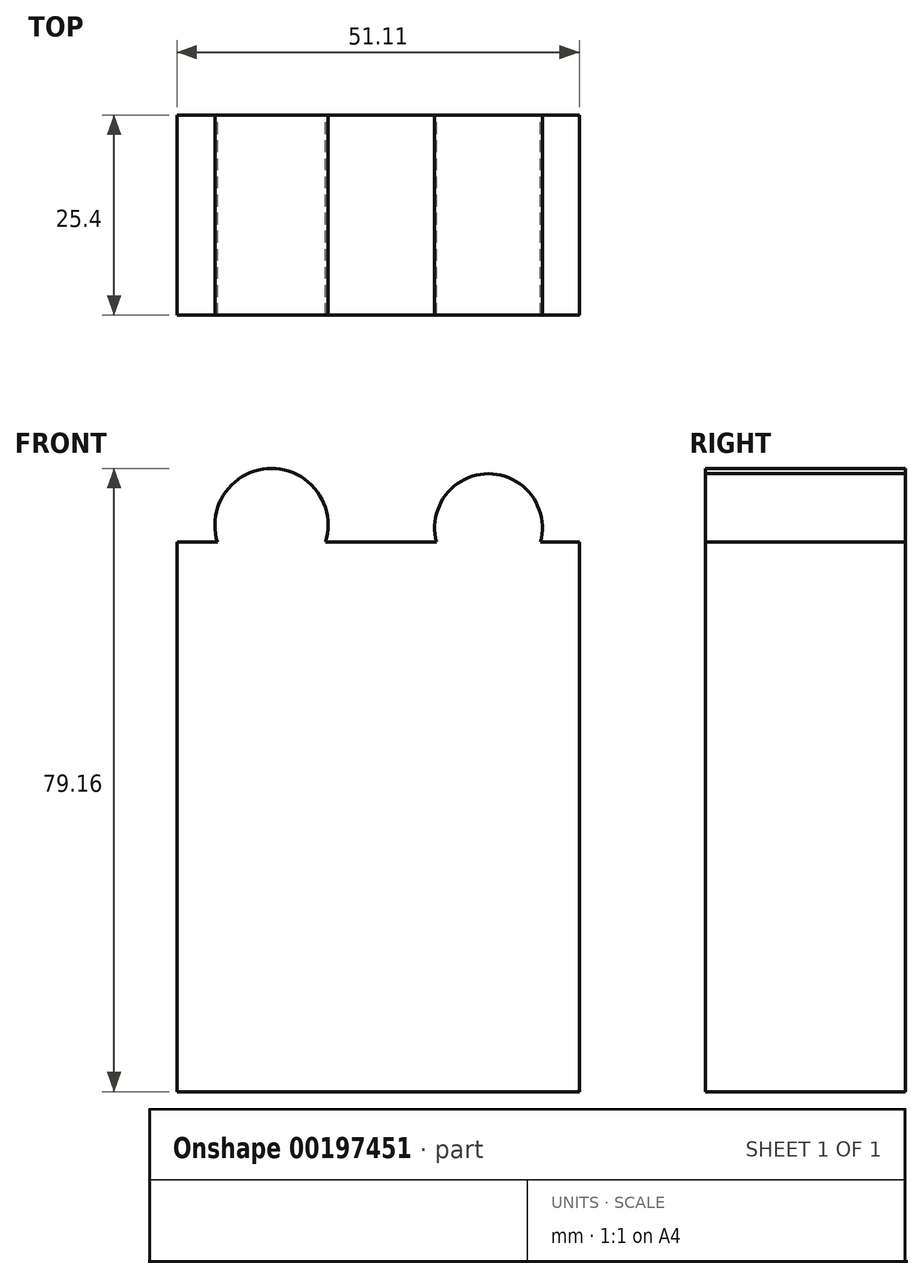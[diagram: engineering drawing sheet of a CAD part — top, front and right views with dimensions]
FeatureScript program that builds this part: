
annotation { "Feature Type Name" : "Feature", "Feature Type Description" : "" }
export const myFeature = defineFeature(function(context is Context, id is Id, definition is map)
    precondition{}
    {
        {
            var Q0;
            Q0=qCreatedBy(makeId("Front.planeOp"),FACE);
            var sketch = newSketch(context, id + "F0", { "sketchPlane" : qUnion([Q0])});
            skLineSegment(sketch, "E0.bottom", {"start": v(-21.93, 34.04) * mm, "end": v(29.18, 34.04) * mm});
            skLineSegment(sketch, "E0.top", {"start": v(-21.93, -35.76) * mm, "end": v(29.18, -35.76) * mm});
            skLineSegment(sketch, "E0.left", {"start": v(-21.93, 34.04) * mm, "end": v(-21.93, -35.76) * mm});
            skLineSegment(sketch, "E0.right", {"start": v(29.18, 34.04) * mm, "end": v(29.18, -35.76) * mm});
            skArc(sketch, "E1", {"start": v(-3.05, 34.04) * mm, "mid": v(-9.92, 43.4) * mm, "end": v(-16.78, 34.04) * mm});
            skArc(sketch, "E2", {"start": v(24.22, 34.04) * mm, "mid": v(17.64, 42.74) * mm, "end": v(11.06, 34.04) * mm});
            skSolve(sketch);
        }
        {
            var Q0;
            Q0 = qSketchRegion(id + "F0", true);
            extrude(context, id + "F1", {"entities" : qUnion([Q0]), "depth" : 25.4 * mm});
        }
    });
